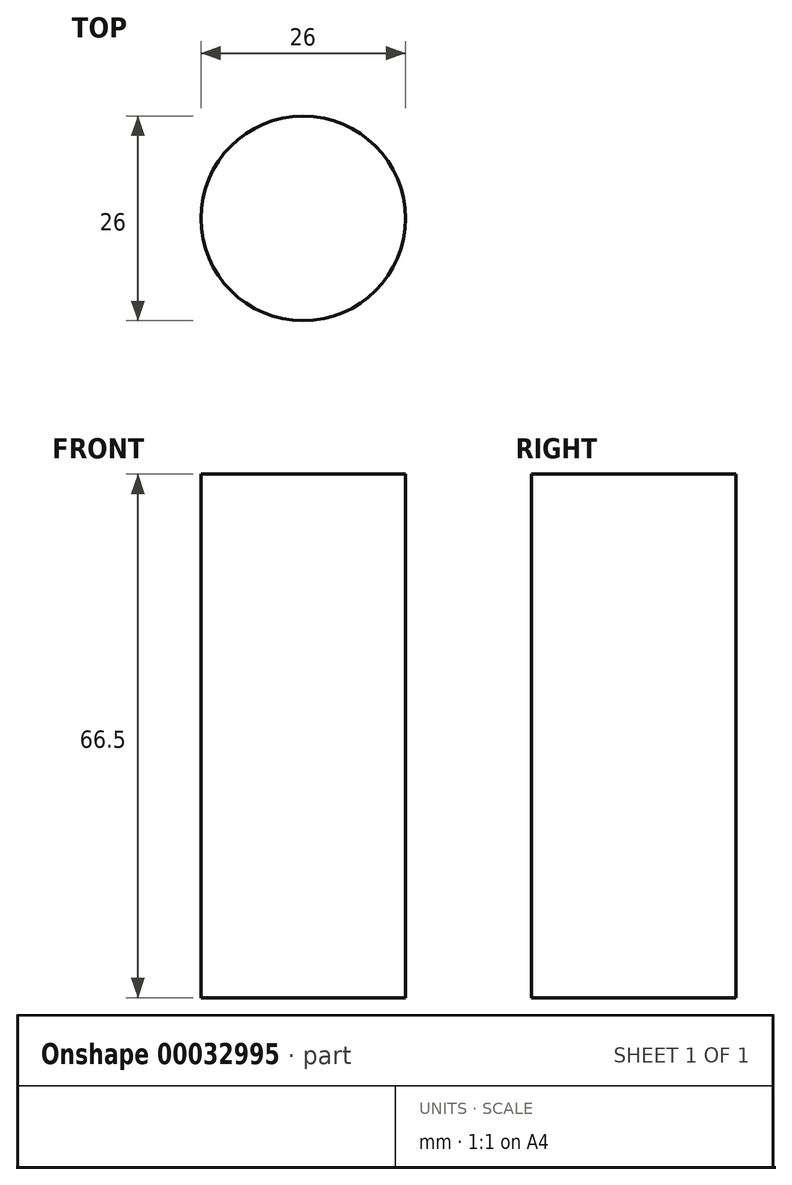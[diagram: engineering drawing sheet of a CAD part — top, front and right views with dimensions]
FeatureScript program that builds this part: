
annotation { "Feature Type Name" : "Feature", "Feature Type Description" : "" }
export const myFeature = defineFeature(function(context is Context, id is Id, definition is map)
    precondition{}
    {
        {
            var Q0;
            Q0=qCreatedBy(makeId("Top.planeOp"),FACE);
            var sketch = newSketch(context, id + "F0", { "sketchPlane" : qUnion([Q0])});
            skCircle(sketch, "E0", {"center": v(0, 0) * mm, "radius": 13 * mm});
            skSolve(sketch);
        }
        {
            var Q0;
            Q0 = qSketchRegion(id + "F0", true);
            extrude(context, id + "F1", {"entities" : qUnion([Q0]), "endBound" : BoundingType.SYMMETRIC, "depth" : 66.5 * mm});
        }
    });
